# Revit family: PRD_AR_ShwrFttngsPckg_F3S-ShowerPanel_F3SV2016 3
name_source: partatom
category: Plumbing Fixtures
units: mm (PartAtom-declared; Revit-internal decimal feet)

## family parameters
Cut with Voids When Loaded = No
Enable Cutting in Views = No
Host = Face
Maintain Annotation Orientation = No
OmniClass Number = 23.45.05.14.17
OmniClass Title = Showers
Part Type = Normal
Room Calculation Point = No
Round Connector Dimension = Use Diameter
Shared = No

## types (1)
- F3SV2016
    AccentColour = chrome-look (glossy)
    AdditionalConnections = no
    AdjustableFlowTime = yes
    AdjustableTiltAngle = yes
    AssetType = Fixed
    BIMObjectName = PRD_AR_ShowerFittingsPackage_F3S-ShowerPanel_F3SV2016
    BasicColour = white
    BodyMaterial = PRD_AR_MineralMaterial_Alpinewhite
    Category = Pr_40_20_87_75, Shower fittings package
    Circulation = no
    Color = alpine white
    Colour = alpine white
    CompatibleA3000Open = no
    ConnectionWithPayWaterDispenser = not possible
    Default Elevation = 1000 mm  [stored 3.28084 ft]
    Description = F3S shower panel made of mineral material for wall mounting with DN 20 self-closing gate valve and waterfall shower. Hydraulically controlled, for connection from above to pre-mixed hot or cold water. Self-closing functional part, piston-free design, self-closing and stepless adjustment of flow duration. Valve housing including shuttle valve seat, visible parts polished chrome-plated. DN 15 waterfall shower with ball joint and rosette. Adjustable jet tilt angle 28°. Polished chromium-plated brass. Housing with raised function surface made of MIRANIT resin-bonded mineral material with pore-free smooth surface (temperature-resistant up to 80°C), Alpine white colour. Connecting hose with lockable water flow regulator and strainer.
    DiameterNominal = 20  [stored 0.0656168 ft]
    DrainSize = 15 mm  [stored 0.0492126 ft]
    Export Type to IFC As = IfcSanitaryTerminalType
    Features = Made of mineral material for wall mounting. For connection from above to pre-mixed hot or cold water. Dimensions of housing 235 x 1160 x 100 mm (W x H x D).
    FittingMaterial = PRD_AR_ChromatedBrass_HighPolished
    Flow = 1.0 L/s
    ForHandShower = no
    FunctionalPrinciple = hydraulic self-closing
    HasTray = No
    HygieneFlushing = no
    IfcExportAs = IfcSanitaryTerminalType
    IfcExportType = SHOWER
    InletSize = DN 20
    LockingMechanism = Top section, non-ceramic
    Manufacturer = KWC Group Management AG
    ManufacturerName = KWC Group Management AG
    ManufacturerURL = www.kwc-professional.com
    Material = mineral material
    MaterialCasing = mineral material
    MaterialCodeCasing = Miranit
    MaterialFitting = brass-look
    MaximumFlowTime = 30 Seconds
    MinimumFlowPressure = 1 bar
    MinimumFlowTime = 5 Seconds
    Model = F3SV2016
    ModelNumber = 3600007159
    ModelReference = F3SV2016
    NBSDescription = Shower fittings package
    NBSReference = 45-35-70/330
    Name = Shower panel made of MIRANIT with waterfall shower F3SV2016
    NominalDepth = 100 mm  [stored 0.328084 ft]
    NominalHeight = 1160 mm  [stored 3.80577 ft]
    NominalLength = 1160 mm  [stored 3.80577 ft]
    NominalWidth = 235 mm  [stored 0.770997 ft]
    OverallDepth = 100 mm
    OverallHeight = 1.160 mm
    OverallWidth = 235 mm
    PositionOfWaterConnection = above
    ProductInformation = http://pim.kwc.com
    ProtectiveShutdown = no
    ShowerHead = with shower head
    ShowerPipeDraining = no
    ShowerType = INDIVIDUAL
    Size = 235 x 1160 x 100 mm (W x H x D)
    SoundInsulation = no
    Status = NEW
    SurfaceFinishFitting = chromed
    SurfaceTreatmentFitting = polished
    TemperatureLimit = no
    ThermalDisinfection = no
    Type IFC Predefined Type = SHOWER
    TypeOfMixing = no
    TypeOfMounting = wall mounting
    TypeOfOperation = manual operation
    TypeOfShower = shower panel
    TypeOfShowerHead = drench shower head
    URL = www.kwc-professional.com
    Uniclass2015Code = Pr_40_20_87_75
    Uniclass2015Title = Shower fittings package
    Uniclass2015Version = Products v1.38
    Version = 1
    VolumeFlowRateAt3Bar = 0.98 l/s
    WaterConnection = hose (gland nut)
    WithBackflowPreventer = no
    WithFilter = yes
    WithRosettesCoverPlate = yes
    WithShowerSet = no
    WithSoapDish = no

note: [stored X ft] marks values corroborated as IEEE doubles in the binary element streams (Revit-internal decimal feet)

## geometry (parser evidence)
native form markers: Sweep x3
no freeform markers — native parametric forms only
